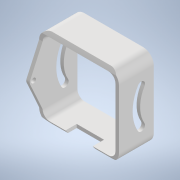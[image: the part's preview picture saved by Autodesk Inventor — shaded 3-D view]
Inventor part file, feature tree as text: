
AUTODESK INVENTOR PART (.ipt)
format: ipt  version: 2022 (Build 260153000, 153)  size: 228,864 bytes
history: native  units: mm
features: reference x9, other x8, extrude x5, sketch x5
ambient origin geometry x8: Origin, YZ Plane, XZ Plane, XY Plane, X Axis, Y Axis, Z Axis, Center Point
bodies: Body1 (feature_tree)
feature tree (27):
  other  "Твердое тело1"
  other  "РабПлоскость1"
  extrude  "Выдавливание1"  Depth=7.0mm
  extrude  "Выдавливание2"  Depth=7.0mm
  extrude  "Выдавливание3"  Depth=7.0mm
  extrude  "Выдавливание5"  Depth=7.0mm
  sketch  "Эскиз6"
  other  "РабПлоскость2"
  extrude  "Выдавливание6"  Depth=0.2mm
  sketch  "Эскиз1"
  reference  "Ссылка1"
  reference  "Ссылка2"
  sketch  "Эскиз2"
  sketch  "Эскиз3"
  reference  "Ссылка3"
  reference  "Ссылка4"
  reference  "Ссылка5"
  sketch  "Эскиз5"
  reference  "Ссылка7"
  reference  "Ссылка8"
  reference  "Ссылка9"
  reference  "Ссылка10"
  other  "<userpath>\Documents\Git\MZCAT_2024\MZCAT_2.iam"
  other  "MZCAT_2.iam"
  other  "LD19:1"
  other  "stabilisator_plan:1"
  other  "lidar_krestovina:1"
